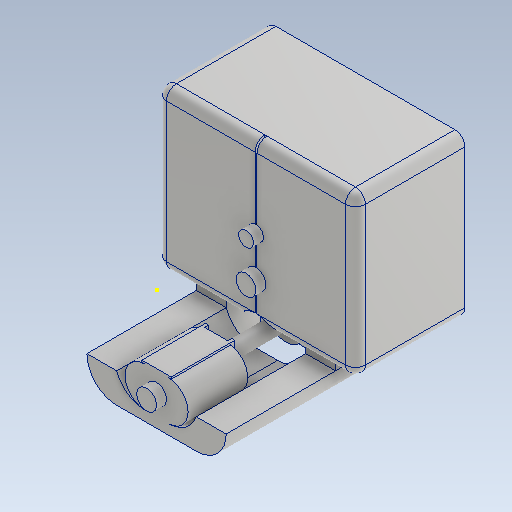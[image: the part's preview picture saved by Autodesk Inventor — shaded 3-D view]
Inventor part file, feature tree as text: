
AUTODESK INVENTOR PART (.ipt)
format: ipt  version: 2021 (Build 250183000, 183)  size: 435,712 bytes
history: native  units: mm
features: sketch x27, extrude x25, fillet x5, plane x2
ambient origin geometry x8: Origin, YZ Plane, XZ Plane, XY Plane, X Axis, Y Axis, Z Axis, Center Point
bodies: Solid1 (feature_tree)
feature tree (59):
  extrude  "Extrusion1"  Depth=80.0mm
  extrude  "Extrusion2"  Depth=50.0mm
  sketch  "Sketch3"  dims[d4=50.0mm d5=0.0mm d6=80.0mm]
  sketch  "Sketch4"  dims[d7=20.0mm d8=0.0mm d9=70.0mm]
  extrude  "Extrusion3"  Depth=50.0mm
  extrude  "Extrusion4"  Depth=70.0mm
  extrude  "Extrusion5"  Depth=20.0mm TaperAngle=0.0deg
  fillet  "Fillet1"  Radius=15.0mm
  sketch  "Sketch7"  dims[d20=40.0mm d21=55.0mm d22=0.0mm]
  extrude  "Extrusion6"  Depth=5.0mm TaperAngle=0.0deg
  fillet  "Fillet2"  Radius=15.0mm
  fillet  "Fillet3"  Radius=10.0mm
  extrude  "Extrusion7"  Depth=55.0mm TaperAngle=0.0deg
  extrude  "Extrusion8"  Depth=15.0mm
  extrude  "Extrusion9"  Depth=90.0mm
  extrude  "Extrusion10"  Depth=45.0mm TaperAngle=0.0deg
  extrude  "Extrusion12"  Depth=5.0mm TaperAngle=0.0deg
  extrude  "Extrusion13"  Depth=5.0mm TaperAngle=0.0deg
  extrude  "Extrusion14"  Depth=21.0mm
  extrude  "Extrusion15"  Depth=2.0mm TaperAngle=0.0deg
  extrude  "Extrusion16"  Depth=1.0mm TaperAngle=0.0deg
  extrude  "Extrusion17"  Depth=10.0mm
  fillet  "Fillet4"  Radius=4.0mm
  plane  "Work Plane1"
  extrude  "Extrusion21"  Depth=10.0mm
  extrude  "Extrusion22"  Depth=5.0mm
  plane  "Work Plane2"
  extrude  "Extrusion23"  Depth=50.0mm TaperAngle=0.0deg
  extrude  "Extrusion24"  TaperAngle=0.0deg  [1 undecoded]
  extrude  "Extrusion25"  Depth=5.0mm
  extrude  "Extrusion26"  Depth=20.0mm
  extrude  "Extrusion27"  Depth=5.0mm TaperAngle=0.0deg
  extrude  "Extrusion28"  Depth=5.0mm TaperAngle=0.0deg
  extrude  "Extrusion29"  Depth=49.75mm
  fillet  "Fillet5"  Radius=7.5mm
  sketch  "Sketch1"  dims[d0=100.0mm d1=80.0mm]
  sketch  "Sketch2"  dims[d2=40.0mm d3=50.0mm]
  sketch  "Sketch5"  dims[d10=15.0mm d11=20.0mm d12=0.0mm d13=15.0mm]
  sketch  "Sketch6"  dims[d14=20.0mm d15=0.0mm d16=5.0mm d17=0.0mm d18=15.0mm d19=10.0mm]
  sketch  "Sketch8"  dims[d23=15.0mm d24=15.0mm]
  sketch  "Sketch9"  dims[d25=30.0mm d26=0.0mm d27=90.0mm]
  sketch  "Sketch10"  dims[d28=70.0mm d29=45.0mm d30=0.0mm]
  sketch  "Sketch11"  dims[d31=10.0mm d32=5.0mm d33=0.0mm]
  sketch  "Sketch12"  dims[d34=7.5mm d35=5.0mm d36=0.0mm]
  sketch  "Sketch14"  dims[d40=1.5mm d41=21.0mm]
  sketch  "Sketch15"  dims[d42=1.5mm d43=2.0mm d44=0.0mm]
  sketch  "Sketch16"  dims[d45=1.5mm d46=1.0mm d47=0.0mm]
  sketch  "Sketch17"  dims[d48=1.0mm d49=0.0mm d50=10.0mm d51=4.0mm d52=0.0mm]
  sketch  "Sketch18"  dims[d53=10.0mm d54=0.0mm d55=7.5mm]
  sketch  "Sketch19"  dims[d56=5.0mm d57=0.0mm d58=5.0mm]
  sketch  "Sketch24"  dims[d59=0.0mm d64=50.0mm d75=17.5mm d76=0.0mm]
  sketch  "Sketch25"  dims[d77=20.0mm d78=0.0mm d79=0.0mm]
  sketch  "Sketch26"  dims[d80=20.0mm d81=0.0mm d85=66.0mm d92=5.0mm]
  sketch  "Sketch29"  dims[d97=40.0mm d98=20.0mm]
  sketch  "Sketch30"  dims[d99=5.0mm d100=0.0mm d101=5.0mm d102=0.0mm]
  sketch  "Sketch31"  dims[d103=40.0mm d105=5.0mm d106=0.0mm]
  sketch  "Sketch32"  dims[d107=49.75mm d108=49.75mm d109=7.5mm]
  sketch  "Sketch33"  dims[d110=20.0mm]
  sketch  "Sketch34"  dims[d111=49.5mm d112=49.5mm d113=5.0mm d114=0.0mm d115=7.5mm d116=10.0mm d117=5.0mm d118=0.0mm d119=10.0mm d120=7.5mm d121=5.0mm d122=0.0mm d123=5.0mm]
note: 1 required parameter value undecoded (feature->parameter linkage not recoverable at this tier; creation-order binding heuristic only, values carry confidence <= 0.55)
